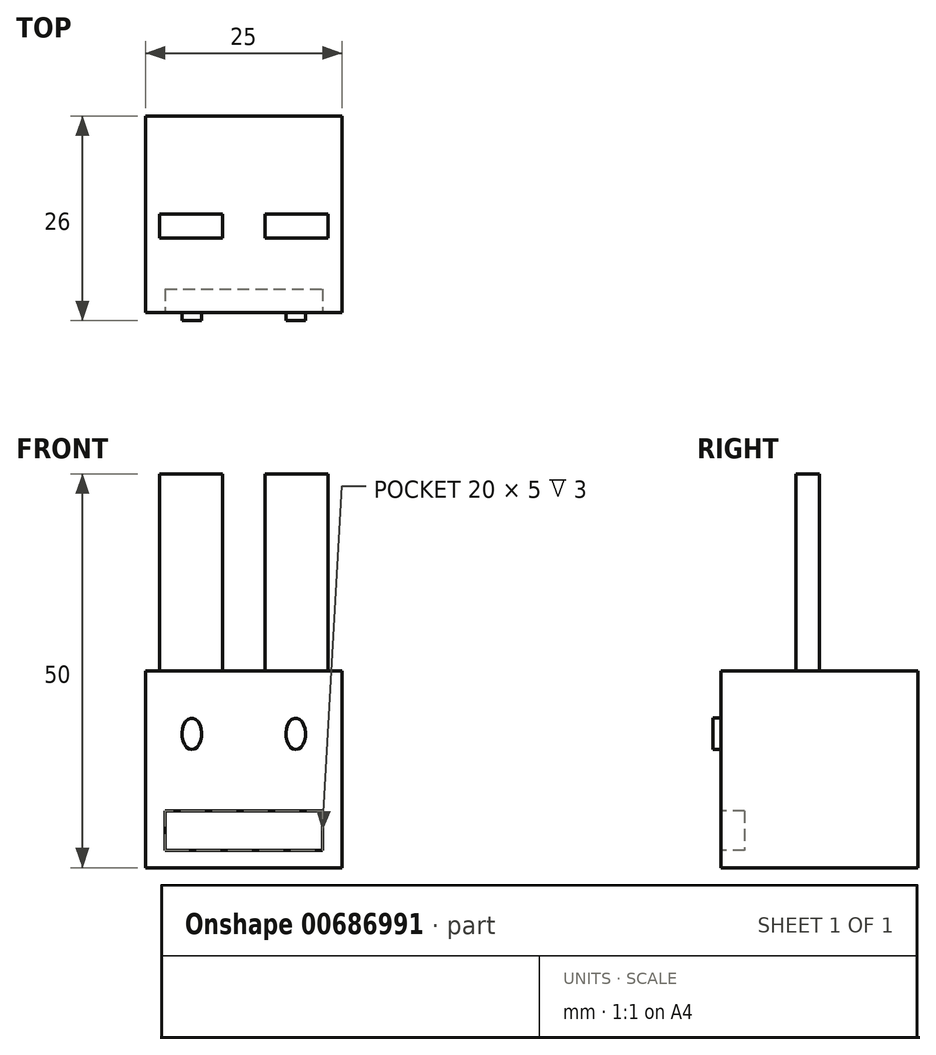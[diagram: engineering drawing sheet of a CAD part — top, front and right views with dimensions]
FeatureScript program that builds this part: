
annotation { "Feature Type Name" : "Feature", "Feature Type Description" : "" }
export const myFeature = defineFeature(function(context is Context, id is Id, definition is map)
    precondition{}
    {
        {
            var Q0;
            Q0=qCreatedBy(makeId("Top.planeOp"),FACE);
            var sketch = newSketch(context, id + "F0", { "sketchPlane" : qUnion([Q0])});
            skLineSegment(sketch, "E0.bottom", {"start": v(12.5, -12.5) * mm, "end": v(-12.5, -12.5) * mm});
            skLineSegment(sketch, "E0.top", {"start": v(12.5, 12.5) * mm, "end": v(-12.5, 12.5) * mm});
            skLineSegment(sketch, "E0.left", {"start": v(12.5, -12.5) * mm, "end": v(12.5, 12.5) * mm});
            skLineSegment(sketch, "E0.right", {"start": v(-12.5, -12.5) * mm, "end": v(-12.5, 12.5) * mm});
            skPoint(sketch, "E0.middle", {"position": v(0, 0) * mm});
            skSolve(sketch);
        }
        {
            var Q0;
            Q0 = qSketchRegion(id + "F0", true);
            extrude(context, id + "F1", {"entities" : qUnion([Q0]), "depth" : 25 * mm, "offsetDistance" : 25 * mm});
        }
        {
            var Q0;
            Q0=makeQuery(id+"F1.opExtrude","CAP_FACE",FACE,{"disambiguationData":[OSD([sQuery(id+"F0.wireOp",EDGE,"E0.bottom"),sQuery(id+"F0.wireOp",EDGE,"E0.top"),sQuery(id+"F0.wireOp",EDGE,"E0.left"),sQuery(id+"F0.wireOp",EDGE,"E0.right")])],"isStart":false});
            var sketch = newSketch(context, id + "F2", { "sketchPlane" : qUnion([Q0])});
            skLineSegment(sketch, "E1.bottom", {"start": v(2.7, 0) * mm, "end": v(10.7, 0) * mm});
            skLineSegment(sketch, "E1.top", {"start": v(2.7, -3) * mm, "end": v(10.7, -3) * mm});
            skLineSegment(sketch, "E1.left", {"start": v(2.7, 0) * mm, "end": v(2.7, -3) * mm});
            skLineSegment(sketch, "E1.right", {"start": v(10.7, 0) * mm, "end": v(10.7, -3) * mm});
            skLineSegment(sketch, "E2.bottom", {"start": v(-2.7, 0) * mm, "end": v(-10.7, 0) * mm});
            skLineSegment(sketch, "E2.top", {"start": v(-2.7, -3) * mm, "end": v(-10.7, -3) * mm});
            skLineSegment(sketch, "E2.left", {"start": v(-2.7, 0) * mm, "end": v(-2.7, -3) * mm});
            skLineSegment(sketch, "E2.right", {"start": v(-10.7, 0) * mm, "end": v(-10.7, -3) * mm});
            skSolve(sketch);
        }
        {
            var Q0;
            Q0 = qSketchRegion(id + "F2", true);
            extrude(context, id + "F3", {"entities" : qUnion([Q0]), "operationType" : NewBodyOperationType.ADD, "depth" : 25 * mm, "offsetDistance" : 25 * mm});
        }
        {
            var Q0;
            Q0=makeQuery(id+"F1.opExtrude","SWEPT_FACE",FACE,{"disambiguationData":[OSD([sQuery(id+"F0.wireOp",EDGE,"E0.bottom")])]});
            var sketch = newSketch(context, id + "F4", { "sketchPlane" : qUnion([Q0])});
            skLineSegment(sketch, "E3.bottom", {"start": v(-10, 7.2) * mm, "end": v(10, 7.2) * mm});
            skLineSegment(sketch, "E3.top", {"start": v(-10, 2.2) * mm, "end": v(10, 2.2) * mm});
            skLineSegment(sketch, "E3.left", {"start": v(-10, 7.2) * mm, "end": v(-10, 2.2) * mm});
            skLineSegment(sketch, "E3.right", {"start": v(10, 7.2) * mm, "end": v(10, 2.2) * mm});
            skPoint(sketch, "E3.middle", {"position": v(0, 4.7) * mm});
            skSolve(sketch);
        }
        {
            var Q0;
            Q0 = qSketchRegion(id + "F4", true);
            extrude(context, id + "F5", {"entities" : qUnion([Q0]), "operationType" : NewBodyOperationType.REMOVE, "oppositeDirection" : true, "depth" : 3 * mm, "offsetDistance" : 25 * mm});
        }
        {
            var Q0;
            Q0=makeQuery(id+"F1.opExtrude","SWEPT_FACE",FACE,{"disambiguationData":[OSD([sQuery(id+"F0.wireOp",EDGE,"E0.bottom")])]});
            var sketch = newSketch(context, id + "F6", { "sketchPlane" : qUnion([Q0])});
            skEllipse(sketch, "E4", {"center": v(-6.6, 17) * mm, "majorRadius": 2 * mm, "minorRadius": 1.25 * mm, "majorAxis": v(0, -1)});
            skEllipse(sketch, "E5", {"center": v(6.6, 17) * mm, "majorRadius": 2 * mm, "minorRadius": 1.25 * mm, "majorAxis": v(0, -1)});
            skSolve(sketch);
        }
        {
            var Q0;
            Q0 = qSketchRegion(id + "F6", true);
            extrude(context, id + "F7", {"entities" : qUnion([Q0]), "operationType" : NewBodyOperationType.ADD, "depth" : 1 * mm, "offsetDistance" : 25 * mm});
        }
    });
